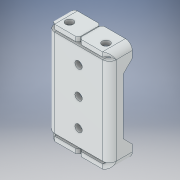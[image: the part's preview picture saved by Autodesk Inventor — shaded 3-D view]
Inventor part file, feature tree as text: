
AUTODESK INVENTOR PART (.ipt)
format: ipt  version: 2018 (Build 220112000, 112)  size: 205,312 bytes
history: native  units: in
note: dims shown in document units (in); Inventor stores cm internally (conversion verified against a paired STEP export)
features: chamfer x1
ambient origin geometry x8: Origin, YZ Plane, XZ Plane, XY Plane, X Axis, Y Axis, Z Axis, Center Point
bodies: Solid1 (feature_tree)
feature tree (1):
  chamfer  "Chamfer3"  [1 undecoded]
note: 1 required parameter value undecoded (feature->parameter linkage not recoverable at this tier; creation-order binding heuristic only, values carry confidence <= 0.55)
